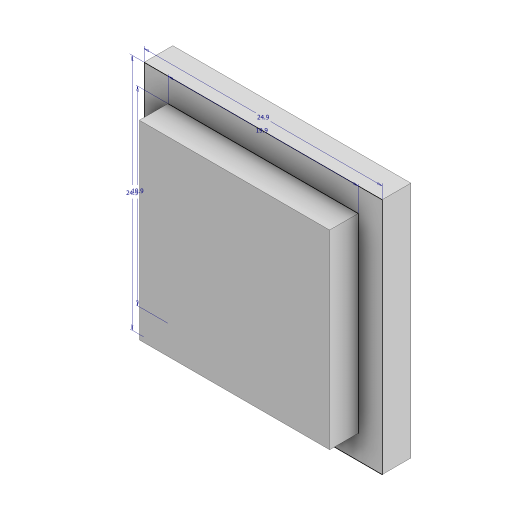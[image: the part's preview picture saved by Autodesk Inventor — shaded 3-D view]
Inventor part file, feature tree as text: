
AUTODESK INVENTOR PART (.ipt)
format: ipt  version: 2023 (Build 270158000, 158)  size: 109,568 bytes
history: native  units: in
note: dims shown in document units (in); Inventor stores cm internally (conversion verified against a paired STEP export)
features: extrude x2
ambient origin geometry x8: Origin, YZ Plane, XZ Plane, XY Plane, X Axis, Y Axis, Z Axis, Center Point
bodies: Solid1 (feature_tree)
feature tree (2):
  extrude  "Extrusion1"  Depth=0.7835in
  extrude  "Extrusion2"  Depth=0.7835in
